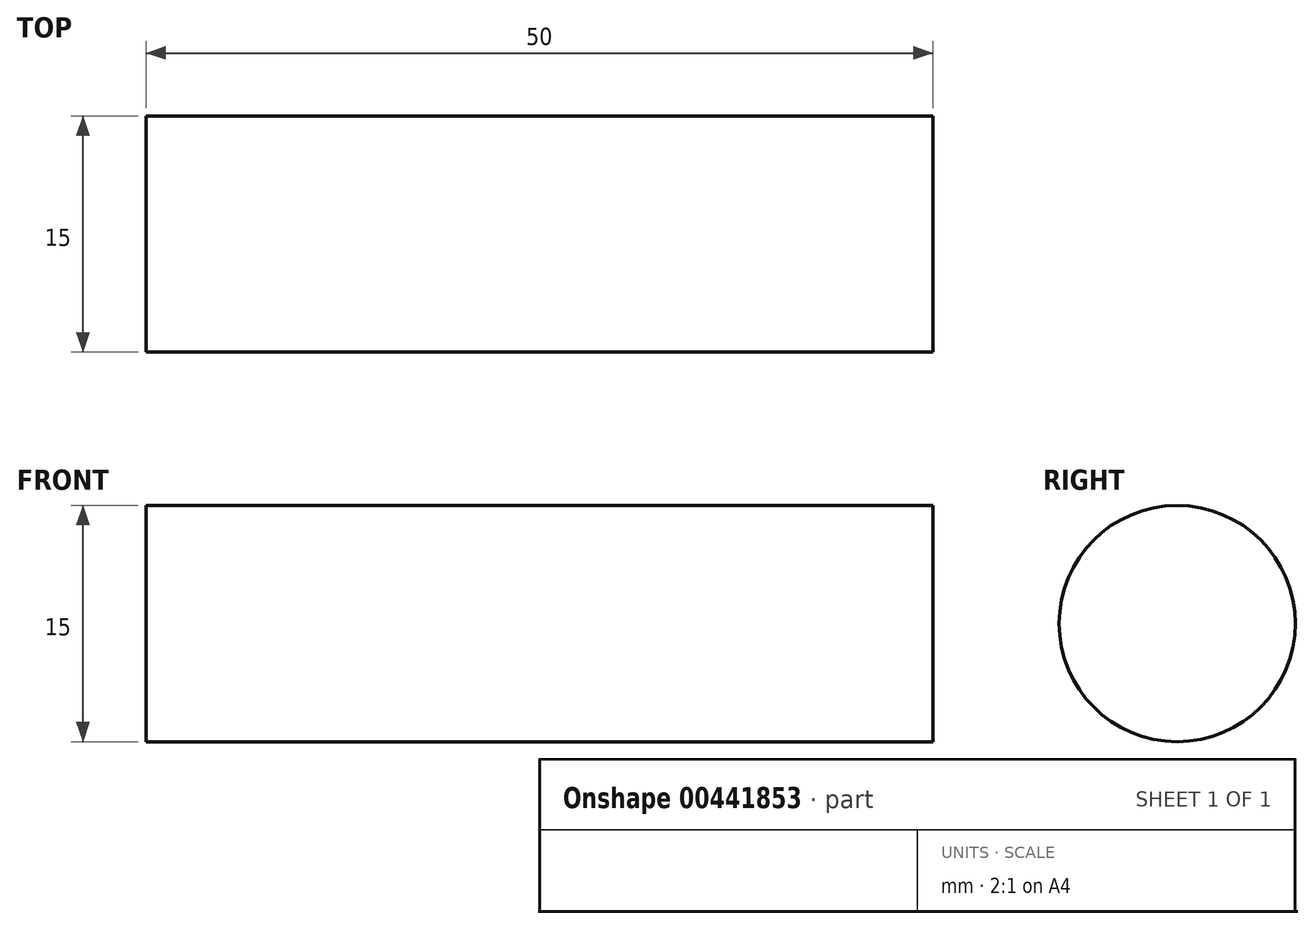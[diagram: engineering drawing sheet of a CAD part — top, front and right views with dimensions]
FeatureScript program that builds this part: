
annotation { "Feature Type Name" : "Feature", "Feature Type Description" : "" }
export const myFeature = defineFeature(function(context is Context, id is Id, definition is map)
    precondition{}
    {
        {
            var Q0;
            Q0=qCreatedBy(makeId("Right.planeOp"),FACE);
            var sketch = newSketch(context, id + "F0", { "sketchPlane" : qUnion([Q0])});
            skCircle(sketch, "E0", {"center": v(0, 0) * mm, "radius": 7.5 * mm});
            skSolve(sketch);
        }
        {
            var Q0;
            Q0 = qSketchRegion(id + "F0", true);
            extrude(context, id + "F1", {"entities" : qUnion([Q0]), "endBound" : BoundingType.SYMMETRIC, "depth" : 50 * mm});
        }
    });
